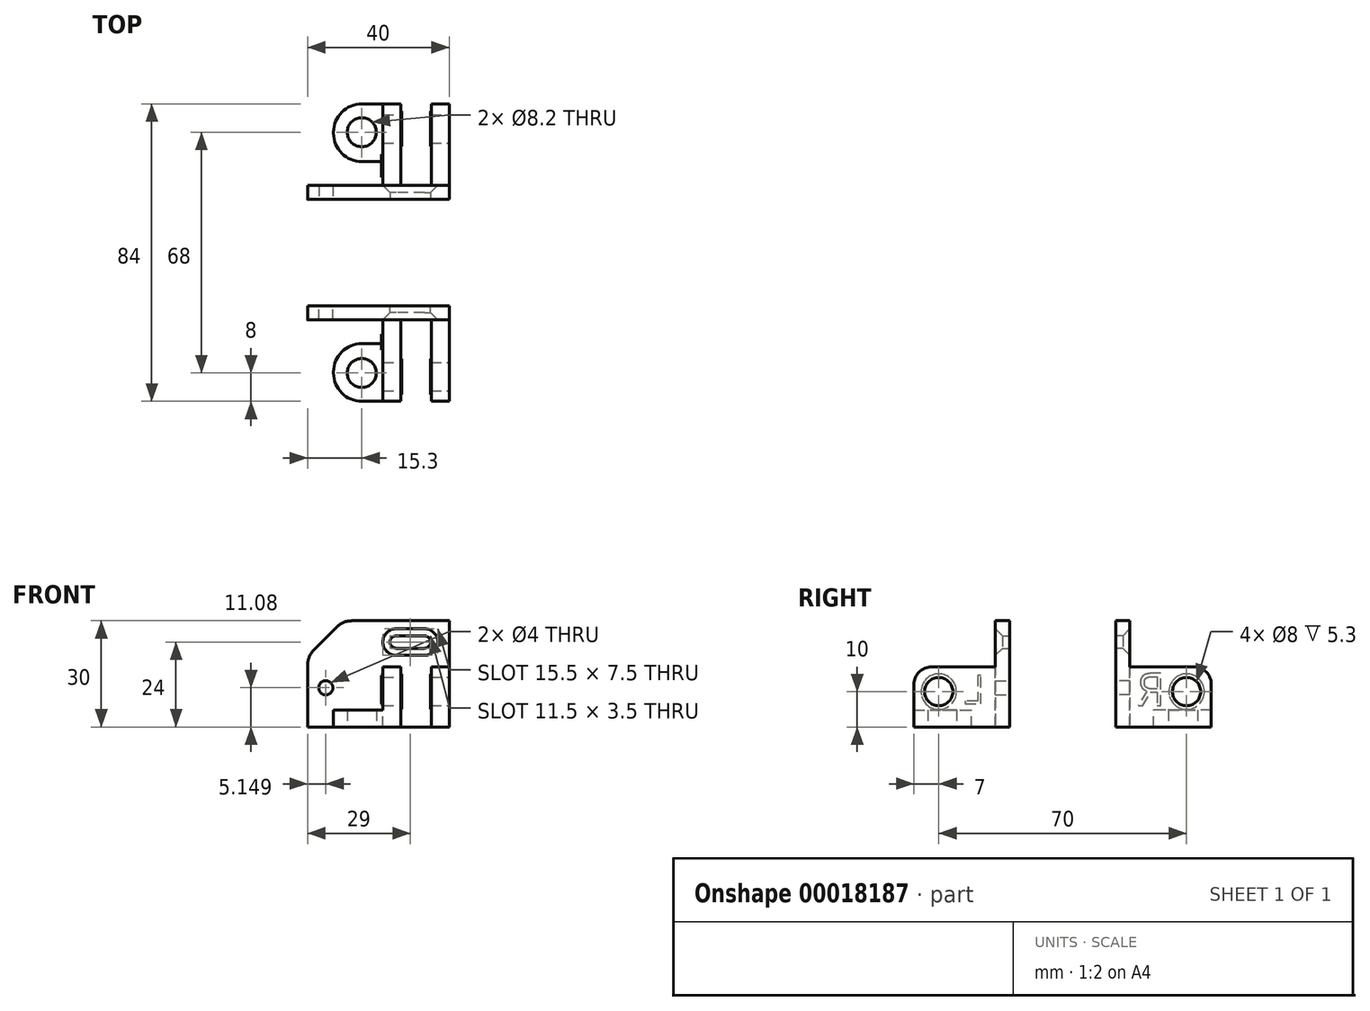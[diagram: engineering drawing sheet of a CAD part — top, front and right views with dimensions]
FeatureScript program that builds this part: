
annotation { "Feature Type Name" : "Feature", "Feature Type Description" : "" }
export const myFeature = defineFeature(function(context is Context, id is Id, definition is map)
    precondition{}
    {
        {
            var Q0;
            Q0=qCreatedBy(makeId("Top.planeOp"),FACE);
            var sketch = newSketch(context, id + "F0", { "sketchPlane" : qUnion([Q0])});
            skLineSegment(sketch, "E0.rect.bottom", {"start": v(-20, 15) * mm, "end": v(20, 15) * mm});
            skLineSegment(sketch, "E0.rect.top", {"start": v(-20, -15) * mm, "end": v(20, -15) * mm});
            skLineSegment(sketch, "E0.rect.left", {"start": v(-20, 15) * mm, "end": v(-20, -15) * mm});
            skLineSegment(sketch, "E0.rect.right", {"start": v(20, 15) * mm, "end": v(20, -15) * mm});
            skPoint(sketch, "E0.rect.middle", {"position": v(0, 0) * mm});
            skLineSegment(sketch, "E1", {"start": v(22.5, 9) * mm, "end": v(-29.72, 9) * mm, "construction": true});
            skLineSegment(sketch, "E2", {"start": v(13, 13.7) * mm, "end": v(13, 4.14) * mm, "construction": true});
            skLineSegment(sketch, "E3", {"start": v(5, 13.23) * mm, "end": v(5, 3.86) * mm, "construction": true});
            skLineSegment(sketch, "E4.bottom", {"start": v(5, 10.75) * mm, "end": v(13, 10.75) * mm});
            skLineSegment(sketch, "E4.top", {"start": v(5, 7.25) * mm, "end": v(13, 7.25) * mm});
            skLineSegment(sketch, "E4.left", {"start": v(5, 10.75) * mm, "end": v(5, 7.25) * mm});
            skLineSegment(sketch, "E4.right", {"start": v(13, 10.75) * mm, "end": v(13, 7.25) * mm});
            skCircle(sketch, "E5", {"center": v(5, 9) * mm, "radius": 1.75 * mm});
            skCircle(sketch, "E6", {"center": v(13, 9) * mm, "radius": 1.75 * mm});
            skLineSegment(sketch, "E7", {"start": v(-14.85, 3.49) * mm, "end": v(-14.85, -10.53) * mm, "construction": true});
            skLineSegment(sketch, "E8", {"start": v(-21.97, -3.92) * mm, "end": v(-8.17, -3.92) * mm, "construction": true});
            skCircle(sketch, "E9", {"center": v(-14.85, -3.92) * mm, "radius": 2 * mm});
            skSolve(sketch);
        }
        {
            var Q0;
            Q0 = qSketchRegion(id + "F0", true);
            extrude(context, id + "F1", {"entities" : qUnion([Q0]), "depth" : 4 * mm});
        }
        {
            var Q0;
            Q0=makeQuery(id+"F1.opExtrude","CAP_EDGE",EDGE,{"disambiguationData":[OSD([sQuery(id+"F0.wireOp",EDGE,"E4.bottom")])],"isStart":false});
            chamfer(context, id + "F2", {"entities" : qUnion([Q0]), "width" : 2 * mm, "tangentPropagation" : true});
        }
        {
            var Q0;
            Q0=makeQuery(id+"F1.opExtrude","SWEPT_EDGE",EDGE,{"disambiguationData":[OSD([sQuery(id+"F0.wireOp",EDGE,"E0.rect.bottom"),sQuery(id+"F0.wireOp",EDGE,"E0.rect.left")])]});
            chamfer(context, id + "F3", {"entities" : qUnion([Q0]), "width" : 10 * mm, "tangentPropagation" : true});
        }
        {
            var Q0;
            {var subQ0=sQuery(id+"F0.wireOp",EDGE,"E0.rect.bottom");Q0=makeQuery(id+"F3.opChamfer","BLEND_EDGE",EDGE,{"blendedFrom":[makeQuery(id+"F1.opExtrude","SWEPT_EDGE",EDGE,{"disambiguationData":[OSD([subQ0,sQuery(id+"F0.wireOp",EDGE,"E0.rect.left")])]}),makeQuery(id+"F1.opExtrude","SWEPT_FACE",FACE,{"disambiguationData":[OSD([subQ0])]})],"blendedInto":[makeQuery(id+"F1.opExtrude","SWEPT_FACE",FACE,{"disambiguationData":[OSD([subQ0])]})]});}
            var Q1;
            {var subQ0=sQuery(id+"F0.wireOp",EDGE,"E0.rect.left");Q1=makeQuery(id+"F3.opChamfer","BLEND_EDGE",EDGE,{"blendedFrom":[makeQuery(id+"F1.opExtrude","SWEPT_EDGE",EDGE,{"disambiguationData":[OSD([sQuery(id+"F0.wireOp",EDGE,"E0.rect.bottom"),subQ0])]}),makeQuery(id+"F1.opExtrude","SWEPT_FACE",FACE,{"disambiguationData":[OSD([subQ0])]})],"blendedInto":[makeQuery(id+"F1.opExtrude","SWEPT_FACE",FACE,{"disambiguationData":[OSD([subQ0])]})]});}
            fillet(context, id + "F4", {"entities" : qUnion([Q0, Q1]), "radius" : 6 * mm, "tangentPropagation" : true, "allowEdgeOverflow" : false});
        }
        {
            var Q0;
            Q0=makeQuery(id+"F1.opExtrude","CAP_FACE",FACE,{"disambiguationData":[OSD([sQuery(id+"F0.wireOp",EDGE,"E0.rect.bottom"),sQuery(id+"F0.wireOp",EDGE,"E0.rect.top"),sQuery(id+"F0.wireOp",EDGE,"E0.rect.left"),sQuery(id+"F0.wireOp",EDGE,"E0.rect.right"),sQuery(id+"F0.wireOp",EDGE,"E4.bottom"),sQuery(id+"F0.wireOp",EDGE,"E4.top"),sQuery(id+"F0.wireOp",EDGE,"E5"),sQuery(id+"F0.wireOp",EDGE,"E6")])],"isStart":false});
            var sketch = newSketch(context, id + "F5", { "sketchPlane" : qUnion([Q0])});
            skLineSegment(sketch, "E10.bottom", {"start": v(20, -15) * mm, "end": v(15, -15) * mm});
            skLineSegment(sketch, "E10.top", {"start": v(20, 2) * mm, "end": v(15, 2) * mm});
            skLineSegment(sketch, "E10.left", {"start": v(20, -15) * mm, "end": v(20, 2) * mm});
            skLineSegment(sketch, "E10.right", {"start": v(15, -15) * mm, "end": v(15, 2) * mm});
            skLineSegment(sketch, "E11.bottom", {"start": v(6.3, -15) * mm, "end": v(1.3, -15) * mm});
            skLineSegment(sketch, "E11.top", {"start": v(6.3, 2) * mm, "end": v(1.3, 2) * mm});
            skLineSegment(sketch, "E11.left", {"start": v(6.3, -15) * mm, "end": v(6.3, 2) * mm});
            skLineSegment(sketch, "E11.right", {"start": v(1.3, -15) * mm, "end": v(1.3, 2) * mm});
            skSolve(sketch);
        }
        {
            var Q0;
            Q0 = qSketchRegion(id + "F5", true);
            extrude(context, id + "F6", {"entities" : qUnion([Q0]), "operationType" : NewBodyOperationType.ADD, "depth" : 23 * mm});
        }
        {
            var Q0;
            Q0=makeQuery(id+"F6.opExtrude","CAP_EDGE",EDGE,{"disambiguationData":[OSD([sQuery(id+"F5.wireOp",EDGE,"E10.top")])],"isStart":false});
            var Q1;
            Q1=makeQuery(id+"F6.opExtrude","CAP_EDGE",EDGE,{"disambiguationData":[OSD([sQuery(id+"F5.wireOp",EDGE,"E11.top")])],"isStart":false});
            var Q2;
            Q2=makeQuery(id+"F6.opExtrude","CAP_EDGE",EDGE,{"disambiguationData":[OSD([sQuery(id+"F5.wireOp",EDGE,"E11.top")])],"isStart":true});
            var Q3;
            Q3=makeQuery(id+"F6.opExtrude","CAP_EDGE",EDGE,{"disambiguationData":[OSD([sQuery(id+"F5.wireOp",EDGE,"E10.top")])],"isStart":true});
            fillet(context, id + "F7", {"entities" : qUnion([Q0, Q1, Q2, Q3]), "radius" : 5 * mm, "tangentPropagation" : true, "allowEdgeOverflow" : false});
        }
        {
            var Q0;
            Q0=makeQuery(id+"F6.boolean.opBoolean","MERGE",FACE,{"derivedFrom":[makeQuery(id+"F1.opExtrude","SWEPT_FACE",FACE,{"disambiguationData":[OSD([sQuery(id+"F0.wireOp",EDGE,"E0.rect.right")])]}),makeQuery(id+"F6.opExtrude","SWEPT_FACE",FACE,{"disambiguationData":[OSD([sQuery(id+"F5.wireOp",EDGE,"E10.left")])]})]});
            var sketch = newSketch(context, id + "F8", { "sketchPlane" : qUnion([Q0])});
            skLineSegment(sketch, "E12", {"start": v(-5, 33.9) * mm, "end": v(-5, -7.2) * mm, "construction": true});
            skLineSegment(sketch, "E13", {"start": v(-23.25, 20) * mm, "end": v(17.75, 20) * mm, "construction": true});
            skCircle(sketch, "E14", {"center": v(-5, 20) * mm, "radius": 4 * mm});
            skSolve(sketch);
        }
        {
            var Q0;
            Q0=sQuery(id+"F8.wireOp",VERTEX,"E14.center");
            var Q1;
            Q1=makeQuery(id+"F1.opExtrude","SWEPT_BODY",BODY,{"disambiguationData":[OSD([sQuery(id+"F0.wireOp",EDGE,"E0.rect.bottom"),sQuery(id+"F0.wireOp",EDGE,"E0.rect.top"),sQuery(id+"F0.wireOp",EDGE,"E0.rect.left"),sQuery(id+"F0.wireOp",EDGE,"E0.rect.right"),sQuery(id+"F0.wireOp",EDGE,"E4.bottom"),sQuery(id+"F0.wireOp",EDGE,"E4.top"),sQuery(id+"F0.wireOp",EDGE,"E5"),sQuery(id+"F0.wireOp",EDGE,"E6")])]});
            hole(context, id + "F9", {"style" : HoleStyle.SIMPLE, "holeDiameter" : 8 * mm, "endStyle" : HoleEndStyle.THROUGH, "locations" : qUnion([Q0]), "scope" : qUnion([Q1])});
        }
        {
            var Q0;
            Q0=makeQuery(id+"F6.opExtrude","SWEPT_FACE",FACE,{"disambiguationData":[OSD([sQuery(id+"F5.wireOp",EDGE,"E11.right")])]});
            var sketch = newSketch(context, id + "F10", { "sketchPlane" : qUnion([Q0])});
            skLineSegment(sketch, "E15.bottom", {"start": v(15, 27) * mm, "end": v(10.2, 27) * mm});
            skLineSegment(sketch, "E15.top", {"start": v(15, 10.7) * mm, "end": v(10.2, 10.7) * mm});
            skLineSegment(sketch, "E15.left", {"start": v(15, 27) * mm, "end": v(15, 10.7) * mm});
            skLineSegment(sketch, "E15.right", {"start": v(10.2, 27) * mm, "end": v(10.2, 10.7) * mm});
            skSolve(sketch);
        }
        {
            var Q0;
            Q0 = qSketchRegion(id + "F10", true);
            extrude(context, id + "F11", {"entities" : qUnion([Q0]), "operationType" : NewBodyOperationType.ADD, "depth" : 14 * mm});
        }
        {
            var Q0;
            Q0=makeQuery(id+"F11.opExtrude","CAP_EDGE",EDGE,{"disambiguationData":[OSD([sQuery(id+"F10.wireOp",EDGE,"E15.bottom")])],"isStart":false});
            var Q1;
            Q1=makeQuery(id+"F11.opExtrude","CAP_EDGE",EDGE,{"disambiguationData":[OSD([sQuery(id+"F10.wireOp",EDGE,"E15.top")])],"isStart":false});
            fillet(context, id + "F12", {"entities" : qUnion([Q0, Q1]), "radius" : 8 * mm, "tangentPropagation" : true, "allowEdgeOverflow" : false});
        }
        {
            var Q0;
            Q0=makeQuery(id+"F11.boolean.opBoolean","MERGE",FACE,{"derivedFrom":[makeQuery(id+"F6.boolean.opBoolean","MERGE",FACE,{"derivedFrom":[makeQuery(id+"F1.opExtrude","SWEPT_FACE",FACE,{"disambiguationData":[OSD([sQuery(id+"F0.wireOp",EDGE,"E0.rect.top")])]}),makeQuery(id+"F6.opExtrude","SWEPT_FACE",FACE,{"disambiguationData":[OSD([sQuery(id+"F5.wireOp",EDGE,"E10.bottom")])]}),makeQuery(id+"F6.opExtrude","SWEPT_FACE",FACE,{"disambiguationData":[OSD([sQuery(id+"F5.wireOp",EDGE,"E11.bottom")])]})]}),makeQuery(id+"F11.opExtrude","SWEPT_FACE",FACE,{"disambiguationData":[OSD([sQuery(id+"F10.wireOp",EDGE,"E15.left")])]})]});
            var sketch = newSketch(context, id + "F13", { "sketchPlane" : qUnion([Q0])});
            skLineSegment(sketch, "E16", {"start": v(-17.14, 19) * mm, "end": v(9.76, 19) * mm, "construction": true});
            skLineSegment(sketch, "E17", {"start": v(-4.7, 31.82) * mm, "end": v(-4.7, 7.57) * mm, "construction": true});
            skCircle(sketch, "E18", {"center": v(-4.7, 19) * mm, "radius": 5.1 * mm});
            skSolve(sketch);
        }
        {
            var Q0;
            Q0=sQuery(id+"F13.wireOp",VERTEX,"E18.center");
            var Q1;
            Q1=makeQuery(id+"F1.opExtrude","SWEPT_BODY",BODY,{"disambiguationData":[OSD([sQuery(id+"F0.wireOp",EDGE,"E0.rect.bottom"),sQuery(id+"F0.wireOp",EDGE,"E0.rect.top"),sQuery(id+"F0.wireOp",EDGE,"E0.rect.left"),sQuery(id+"F0.wireOp",EDGE,"E0.rect.right"),sQuery(id+"F0.wireOp",EDGE,"E4.bottom"),sQuery(id+"F0.wireOp",EDGE,"E4.top"),sQuery(id+"F0.wireOp",EDGE,"E5"),sQuery(id+"F0.wireOp",EDGE,"E6")])]});
            hole(context, id + "F14", {"style" : HoleStyle.SIMPLE, "holeDiameter" : 8.2 * mm, "endStyle" : HoleEndStyle.THROUGH, "locations" : qUnion([Q0]), "scope" : qUnion([Q1])});
        }
        {
            var Q0;
            Q0=makeQuery(id+"F1.opExtrude","SWEPT_BODY",BODY,{"disambiguationData":[OSD([sQuery(id+"F0.wireOp",EDGE,"E0.rect.bottom"),sQuery(id+"F0.wireOp",EDGE,"E0.rect.top"),sQuery(id+"F0.wireOp",EDGE,"E0.rect.left"),sQuery(id+"F0.wireOp",EDGE,"E0.rect.right"),sQuery(id+"F0.wireOp",EDGE,"E4.bottom"),sQuery(id+"F0.wireOp",EDGE,"E4.top"),sQuery(id+"F0.wireOp",EDGE,"E5"),sQuery(id+"F0.wireOp",EDGE,"E6"),sQuery(id+"F0.wireOp",EDGE,"E9")])]});
            var Q1;
            Q1=makeQuery(id+"F1.opExtrude","CAP_EDGE",EDGE,{"disambiguationData":[OSD([sQuery(id+"F0.wireOp",EDGE,"E0.rect.top")])],"isStart":true});
            transform(context, id + "F15", {"entities" : qUnion([Q0]), "transformType" : TransformType.ROTATION, "transformAxis" : qUnion([Q1]), "angle" : 90 * degree, "makeCopy" : false});
        }
        {
            var Q0;
            Q0=makeQuery(id+"F6.opExtrude","SWEPT_FACE",FACE,{"disambiguationData":[OSD([sQuery(id+"F5.wireOp",EDGE,"E10.right")])]});
            var sketch = newSketch(context, id + "F16", { "sketchPlane" : qUnion([Q0])});
            skCircle(sketch, "E19", {"center": v(35, 10) * mm, "radius": 5 * mm});
            skSolve(sketch);
        }
        {
            var Q0;
            Q0=makeQuery(id+"F16.imprint","IMPRINT",FACE,{"disambiguationData":[TD([[makeQuery(id+"F16.imprint","IMPRINT",EDGE,{"derivedFrom":sQuery(id+"F16.wireOp",EDGE,"E19")}),1.0]])]});
            extrude(context, id + "F17", {"entities" : qUnion([Q0]), "operationType" : NewBodyOperationType.ADD, "depth" : 0.3 * mm});
        }
        {
            var Q0;
            Q0=makeQuery(id+"F6.opExtrude","SWEPT_FACE",FACE,{"disambiguationData":[OSD([sQuery(id+"F5.wireOp",EDGE,"E11.left")])]});
            var sketch = newSketch(context, id + "F18", { "sketchPlane" : qUnion([Q0])});
            skCircle(sketch, "E20", {"center": v(-35, 10) * mm, "radius": 5 * mm});
            skSolve(sketch);
        }
        {
            var Q0;
            Q0=makeQuery(id+"F18.imprint","IMPRINT",FACE,{"disambiguationData":[TD([[makeQuery(id+"F18.imprint","IMPRINT",EDGE,{"derivedFrom":sQuery(id+"F18.wireOp",EDGE,"E20")}),1.0]])]});
            extrude(context, id + "F19", {"entities" : qUnion([Q0]), "operationType" : NewBodyOperationType.ADD, "depth" : 0.3 * mm});
        }
        {
            var Q0;
            Q0=makeQuery(id+"F1.opExtrude","SWEPT_BODY",BODY,{"disambiguationData":[OSD([sQuery(id+"F0.wireOp",EDGE,"E0.rect.bottom"),sQuery(id+"F0.wireOp",EDGE,"E0.rect.top"),sQuery(id+"F0.wireOp",EDGE,"E0.rect.left"),sQuery(id+"F0.wireOp",EDGE,"E0.rect.right"),sQuery(id+"F0.wireOp",EDGE,"E4.bottom"),sQuery(id+"F0.wireOp",EDGE,"E4.top"),sQuery(id+"F0.wireOp",EDGE,"E5"),sQuery(id+"F0.wireOp",EDGE,"E6"),sQuery(id+"F0.wireOp",EDGE,"E9")])]});
            var Q1;
            Q1=qCreatedBy(makeId("Front.planeOp"),FACE);
            mirror(context, id + "F20", {"entities" : qUnion([Q0]), "mirrorPlane" : qUnion([Q1])});
        }
        {
            var Q0;
            Q0=makeQuery(id+"F6.opExtrude","SWEPT_FACE",FACE,{"disambiguationData":[OSD([sQuery(id+"F5.wireOp",EDGE,"E11.right")])]});
            var sketch = newSketch(context, id + "F21", { "sketchPlane" : qUnion([Q0])});
            skText(sketch, "E21", { "text": "L", "fontName": "OpenSans-Regular.ttf"});
            const initialGuessF21  = {"E21": [0.02194, 0.00652, 1, 0, 0.00807]};
            skSetInitialGuess(sketch, initialGuessF21);
            skSolve(sketch);
        }
        {
            var Q0;
            Q0 = qSketchRegion(id + "F21", true);
            extrude(context, id + "F22", {"entities" : qUnion([Q0]), "operationType" : NewBodyOperationType.ADD, "depth" : 0.5 * mm});
        }
        {
            var Q0;
            Q0=makeQuery(id+"F20.opPattern","COPY",FACE,{"derivedFrom":makeQuery(id+"F6.opExtrude","SWEPT_FACE",FACE,{"disambiguationData":[OSD([sQuery(id+"F5.wireOp",EDGE,"E11.right")])]}),"instanceName":"1"});
            var sketch = newSketch(context, id + "F23", { "sketchPlane" : qUnion([Q0])});
            skText(sketch, "E22", { "text": "R", "fontName": "OpenSans-Regular.ttf"});
            const initialGuessF23  = {"E22": [-0.02902, 0.00603, 1, 0, 0.00921]};
            skSetInitialGuess(sketch, initialGuessF23);
            skSolve(sketch);
        }
        {
            var Q0;
            Q0 = qSketchRegion(id + "F23", true);
            extrude(context, id + "F24", {"entities" : qUnion([Q0]), "operationType" : NewBodyOperationType.ADD, "depth" : 0.5 * mm});
        }
    });
